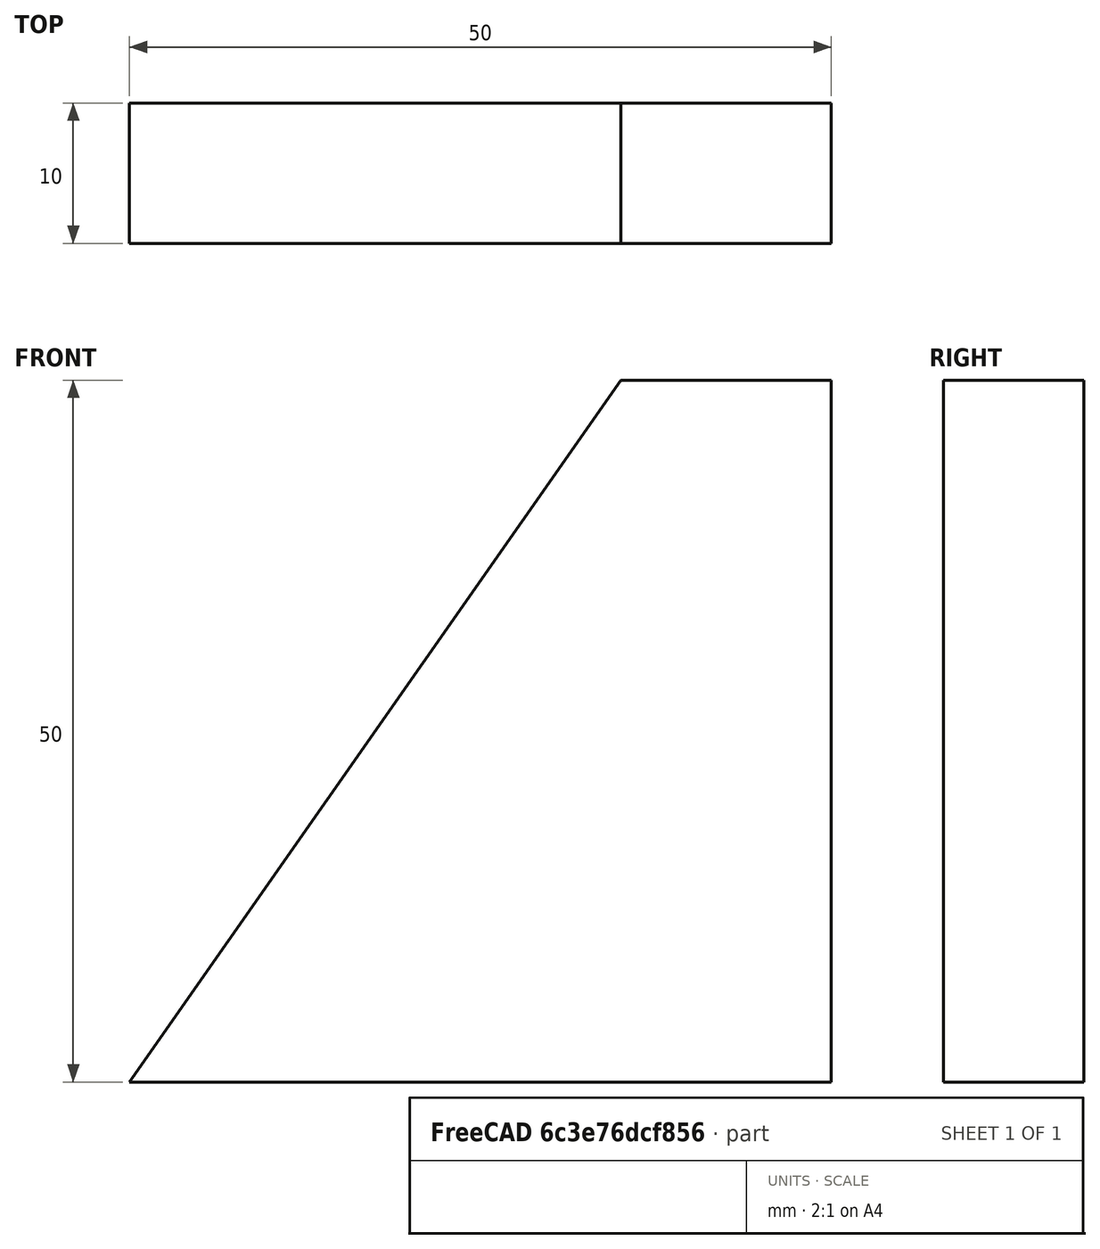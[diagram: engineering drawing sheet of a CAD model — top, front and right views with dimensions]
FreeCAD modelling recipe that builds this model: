
FCSTD DOCUMENT  (FreeCAD 0.18.4R)
Label: cannon-support
License: All rights reserved
LicenseURL: http://en.wikipedia.org/wiki/All_rights_reserved
objects: Sketcher::SketchObject×1, PartDesign::Pad×1, PartDesign::Body×1
note: 4 computed .brp shape members not serialized (recipe doc carries the construction recipe); baked Part::Feature solids carry a one-line shape summary decoded from their .brp

FEATURE [Sketcher::SketchObject] Sketch
  MapMode = 5
  Placement = pos=(0,0,0) rot=(1,0,0;1.5708rad)
  Support = -> [XZ_Plane]
  sketch-geometry (4):
    g0: LineSegment StartX=0 StartY=0 StartZ=0 EndX=35 EndY=50 EndZ=0
    g1: LineSegment StartX=35 StartY=50 StartZ=0 EndX=50 EndY=50 EndZ=0
    g2: LineSegment StartX=50 StartY=50 StartZ=0 EndX=50 EndY=0 EndZ=0
    g3: LineSegment StartX=50 StartY=0 StartZ=0 EndX=0 EndY=0 EndZ=0
  constraints (11):
    c: Coincident(g-1,g0)
    c: Coincident(g0,g1)
    c: Horizontal(g1)
    c: Coincident(g1,g2)
    c: PointOnObject(g2,g-1)
    c: Vertical(g2)
    c: Coincident(g2,g3)
    c: Coincident(g3,g0)
    c: DistanceX(g3,g3) = 50
    c: DistanceY(g2,g2) = 50
    c: DistanceX(g1,g1) = 15
FEATURE [PartDesign::Pad] Pad
  Length = 10
  Length2 = 100
  Placement = pos=(0,0,0) rot=(1,0,0;1.5708rad)
  Profile = -> Sketch
  Type = 0
FEATURE [PartDesign::Body] Body
  Group = -> [Sketch,Pad]
  Origin = -> Origin
  Tip = -> Pad
